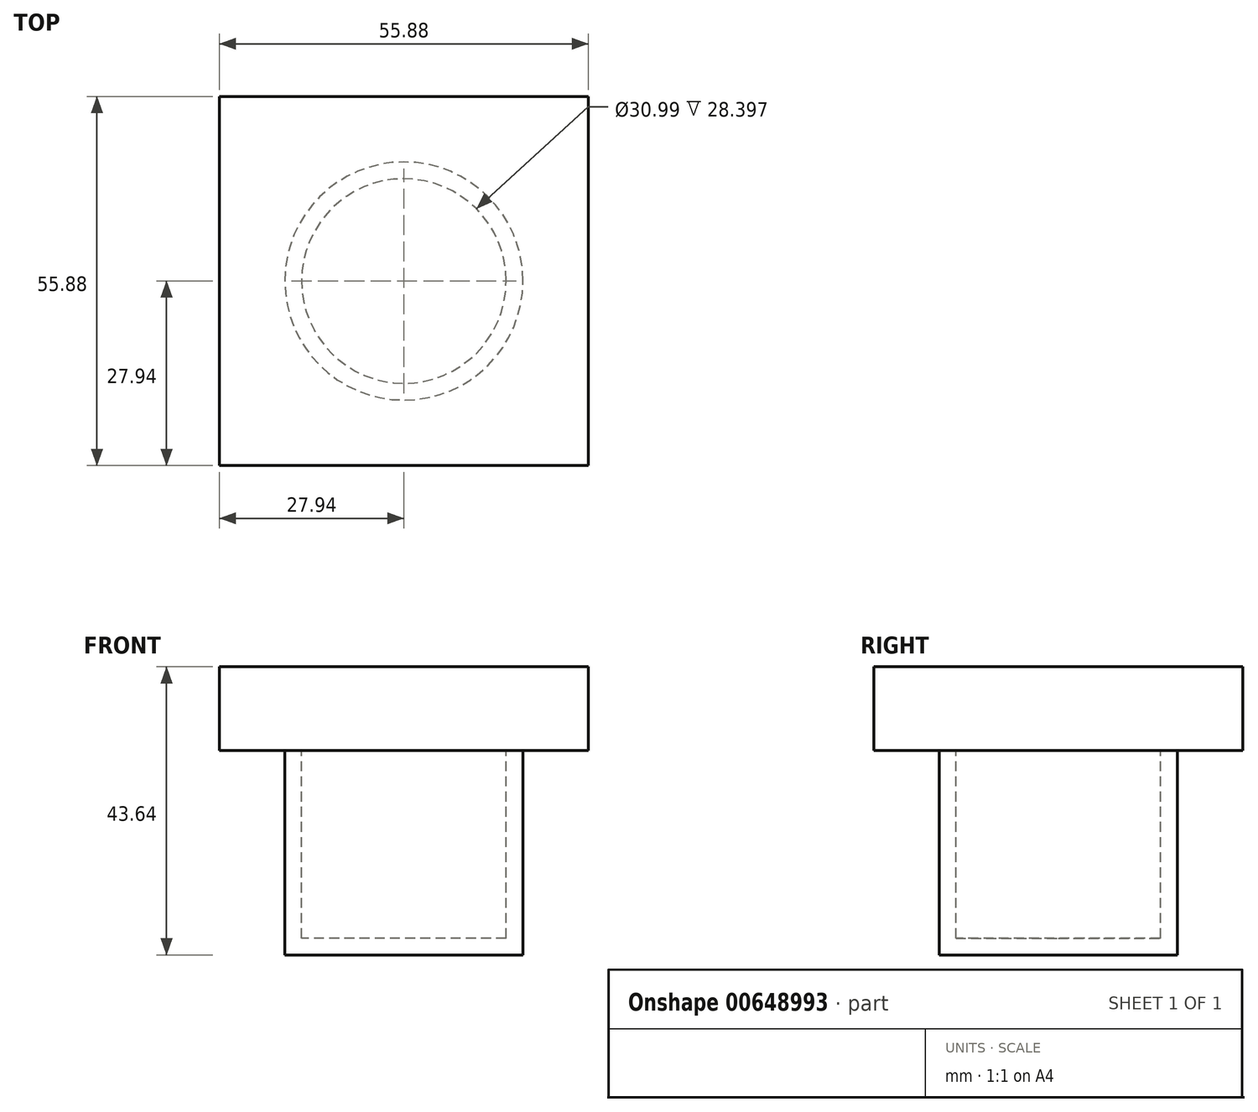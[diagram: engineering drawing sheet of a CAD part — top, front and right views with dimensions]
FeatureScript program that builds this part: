
annotation { "Feature Type Name" : "Feature", "Feature Type Description" : "" }
export const myFeature = defineFeature(function(context is Context, id is Id, definition is map)
    precondition{}
    {
        {
            var Q0;
            Q0=qCreatedBy(makeId("Top.planeOp"),FACE);
            var sketch = newSketch(context, id + "F0", { "sketchPlane" : qUnion([Q0])});
            skLineSegment(sketch, "E0.bottom", {"start": v(27.94, -27.94) * mm, "end": v(-27.94, -27.94) * mm});
            skLineSegment(sketch, "E0.top", {"start": v(27.94, 27.94) * mm, "end": v(-27.94, 27.94) * mm});
            skLineSegment(sketch, "E0.left", {"start": v(27.94, -27.94) * mm, "end": v(27.94, 27.94) * mm});
            skLineSegment(sketch, "E0.right", {"start": v(-27.94, -27.94) * mm, "end": v(-27.94, 27.94) * mm});
            skPoint(sketch, "E0.middle", {"position": v(0, 0) * mm});
            skCircle(sketch, "E1", {"center": v(0, 0) * mm, "radius": 18.03 * mm});
            skSolve(sketch);
        }
        {
            var Q0;
            Q0=makeQuery(id+"F0.imprint","IMPRINT",FACE,{"disambiguationData":[TD([[makeQuery(id+"F0.imprint","IMPRINT",EDGE,{"derivedFrom":sQuery(id+"F0.wireOp",EDGE,"E1")}),1.0]])]});
            extrude(context, id + "F1", {"entities" : qUnion([Q0]), "oppositeDirection" : true, "depth" : 30.94 * mm, "offsetDistance" : 25.4 * mm});
        }
        {
            var Q0;
            Q0=makeQuery(id+"F1.opExtrude","CAP_FACE",FACE,{"disambiguationData":[OSD([sQuery(id+"F0.wireOp",EDGE,"E1")])],"isStart":true});
            shell(context, id + "F2", {"entities" : qUnion([Q0]), "thickness" : 2.54 * mm});
        }
        {
            var Q0;
            Q0=makeQuery(id+"F0.imprint","IMPRINT",FACE,{"disambiguationData":[TD([[makeQuery(id+"F0.imprint","IMPRINT",EDGE,{"derivedFrom":sQuery(id+"F0.wireOp",EDGE,"E0.bottom")}),-1.0]])]});
            var Q1;
            Q1=makeQuery(id+"F0.imprint","IMPRINT",FACE,{"disambiguationData":[TD([[makeQuery(id+"F0.imprint","IMPRINT",EDGE,{"derivedFrom":sQuery(id+"F0.wireOp",EDGE,"E1")}),1.0]])]});
            extrude(context, id + "F3", {"entities" : qUnion([Q0, Q1]), "operationType" : NewBodyOperationType.ADD, "depth" : 12.7 * mm, "offsetDistance" : 25.4 * mm});
        }
    });
